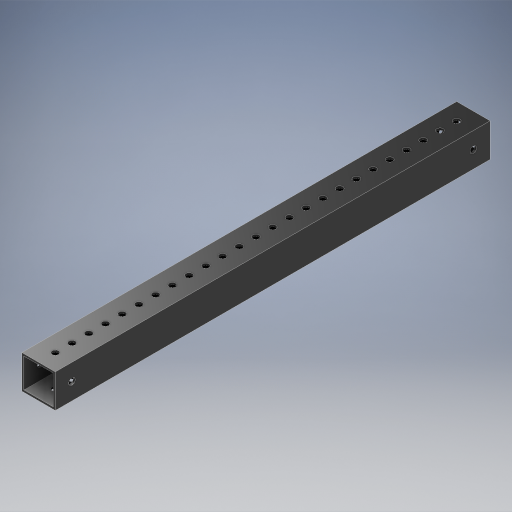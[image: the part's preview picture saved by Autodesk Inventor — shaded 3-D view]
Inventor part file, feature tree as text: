
AUTODESK INVENTOR PART (.ipt)
format: ipt  version: 2024.2 (Build 282272000, 272)  size: 788,992 bytes
history: native  units: in
note: dims shown in document units (in); Inventor stores cm internally (conversion verified against a paired STEP export)
features: other x13, extrude x9, hole x3, pattern_linear x3, mirror x3, sheet_metal_op x1, plane x1
ambient origin geometry x8: Origin, YZ Plane, XZ Plane, XY Plane, X Axis, Y Axis, Z Axis, Center Point
bodies: Solid1 (feature_tree)
feature tree (33):
  other  "Blocks"
  other  "Base Sketch"
  extrude  "Base"  Depth=1.0in
  extrude  "MAX Corner"  Depth=1.0in
  extrude  "MAX Corner Cut"  Depth=0.0625in
  extrude  "Scribe Lines"  Depth=0.0625in
  other  "Side Middle"
  other  "Top Middle"
  other  "Side Holes Sketch"
  hole  "Top Side Hole"  [1 undecoded]
  hole  "Mid Side Hole"  [1 undecoded]
  hole  "Btm Side Hole"  [1 undecoded]
  pattern_linear  "Side Holes"  Spacing1=0.04in  [1 undecoded]
  mirror  "Side Mirror"
  extrude  "MAXTube Hole"  Depth=0.04in
  extrude  "MAXTube Outside"  Depth=13.0in
  pattern_linear  "MAXTube Pattern"  Spacing1=0.0in  [1 undecoded]
  mirror  "MAXTube Mirror"
  extrude  "Left Top Hole"  Depth=13.0in
  extrude  "Mid Top Hole"  TaperAngle=0.0deg  [1 undecoded]
  extrude  "Right Top Hole"  TaperAngle=0.0deg  [1 undecoded]
  pattern_linear  "Top Holes"  Spacing1=0.005in  [1 undecoded]
  mirror  "Top Mirror"
  sheet_metal_op  "Corner"
  other  "MAXTube"
  plane  "Work Plane3"
  other  "Corner:5"
  other  "Corner:6"
  other  "Corner:7"
  other  "Corner:8"
  other  "MAXTube:1"
  other  "MAXTube:2"
  other  "MAXTube:3"
note: 8 required parameter values undecoded (feature->parameter linkage not recoverable at this tier; creation-order binding heuristic only, values carry confidence <= 0.55)
